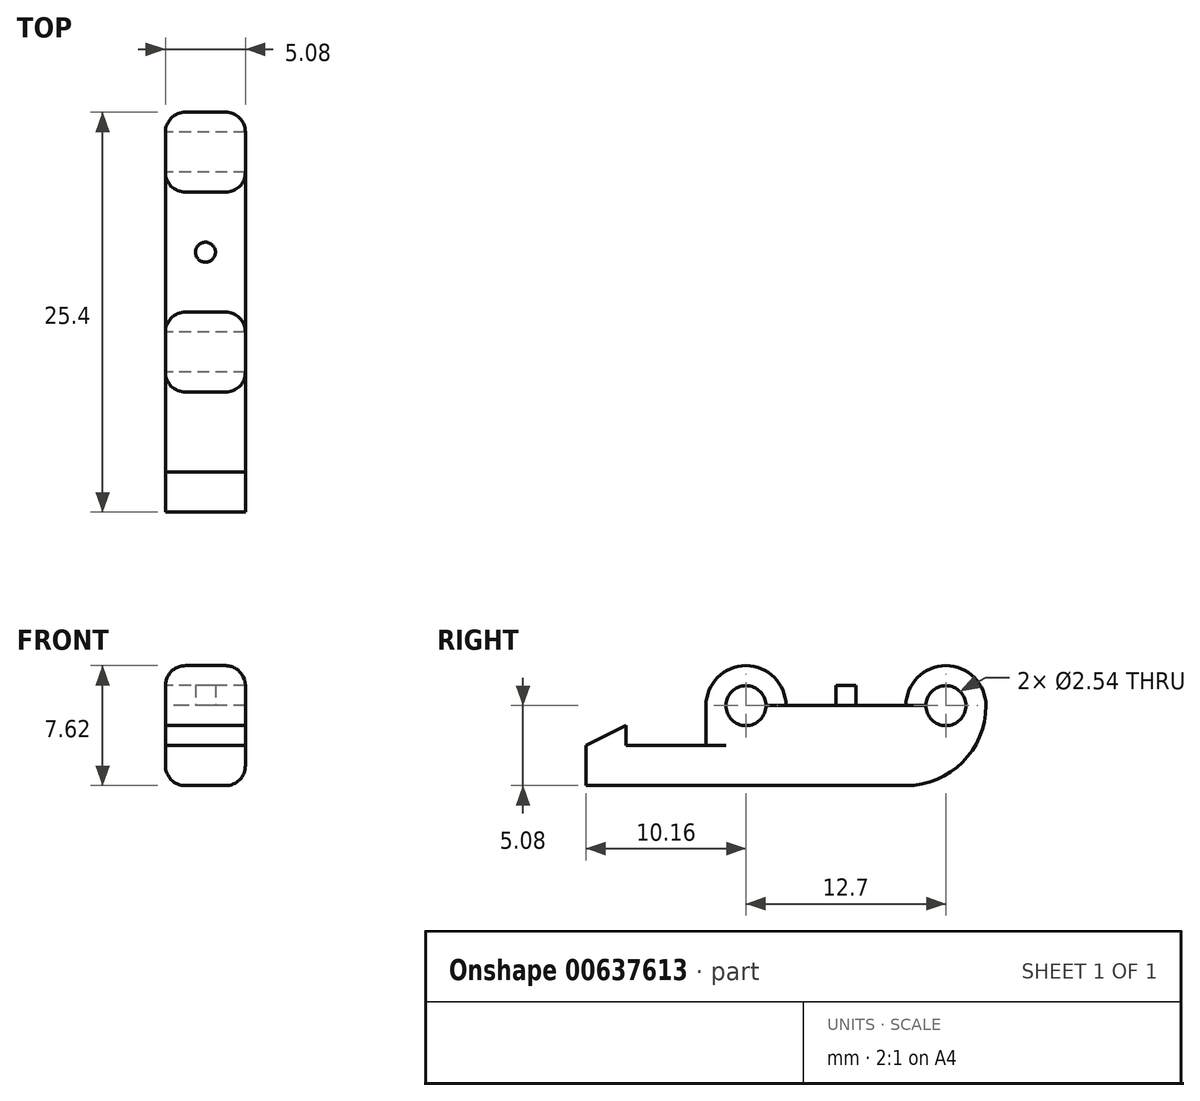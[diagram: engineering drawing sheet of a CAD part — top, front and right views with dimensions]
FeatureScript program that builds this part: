
annotation { "Feature Type Name" : "Feature", "Feature Type Description" : "" }
export const myFeature = defineFeature(function(context is Context, id is Id, definition is map)
    precondition{}
    {
        {
            var Q0;
            Q0=qCreatedBy(makeId("Right.planeOp"),FACE);
            var sketch = newSketch(context, id + "F0", { "sketchPlane" : qUnion([Q0])});
            skCircle(sketch, "E0", {"center": v(0, 0) * mm, "radius": 2.54 * mm});
            skCircle(sketch, "E1", {"center": v(0, 0) * mm, "radius": 1.27 * mm});
            skLineSegment(sketch, "E2", {"start": v(-2.54, 0) * mm, "end": v(-2.54, -5.08) * mm});
            skLineSegment(sketch, "E3", {"start": v(-2.54, -5.08) * mm, "end": v(15.24, -5.08) * mm});
            skLineSegment(sketch, "E4", {"start": v(15.24, -5.08) * mm, "end": v(15.24, 0) * mm});
            skCircle(sketch, "E5", {"center": v(12.7, 0) * mm, "radius": 2.54 * mm});
            skCircle(sketch, "E6", {"center": v(12.7, 0) * mm, "radius": 1.27 * mm});
            skLineSegment(sketch, "E7", {"start": v(10.16, 0) * mm, "end": v(10.16, 0) * mm});
            skLineSegment(sketch, "E8", {"start": v(2.54, 0) * mm, "end": v(2.54, 0) * mm});
            skLineSegment(sketch, "E9", {"start": v(2.54, 0) * mm, "end": v(10.16, 0) * mm});
            skLineSegment(sketch, "E10", {"start": v(-2.54, -5.08) * mm, "end": v(-10.16, -5.08) * mm});
            skLineSegment(sketch, "E11", {"start": v(-10.16, -5.08) * mm, "end": v(-10.16, -2.54) * mm});
            skLineSegment(sketch, "E12", {"start": v(-10.16, -2.54) * mm, "end": v(-2.54, -2.54) * mm});
            skLineSegment(sketch, "E13", {"start": v(-10.16, -2.54) * mm, "end": v(-7.62, -1.27) * mm});
            skLineSegment(sketch, "E14", {"start": v(-7.62, -1.27) * mm, "end": v(-7.62, -2.54) * mm});
            skSolve(sketch);
        }
        {
            var Q0;
            Q0=qSketchRegion(id+"F0",true);
            extrude(context, id + "F1", {"entities" : qUnion([Q0]), "depth" : 5.08 * mm});
        }
        {
            var Q0;
            Q0=makeQuery(id+"F1.opExtrude","SWEPT_FACE",FACE,{"disambiguationData":[OSD([sQuery(id+"F0.wireOp",EDGE,"E9")])]});
            var sketch = newSketch(context, id + "F2", { "sketchPlane" : qUnion([Q0])});
            skCircle(sketch, "E15", {"center": v(2.54, 6.35) * mm, "radius": 0.64 * mm});
            skPoint(sketch, "E15.centerSnap0", {"position": v(0, 6.35) * mm});
            skSolve(sketch);
        }
        {
            var Q0;
            Q0=qSketchRegion(id+"F2",true);
            extrude(context, id + "F3", {"entities" : qUnion([Q0]), "operationType" : NewBodyOperationType.ADD, "depth" : 1.27 * mm});
        }
        {
            var Q0;
            Q0=makeQuery(id+"F1.opExtrude","SWEPT_EDGE",EDGE,{"disambiguationData":[OSD([sQuery(id+"F0.wireOp",EDGE,"E3"),sQuery(id+"F0.wireOp",EDGE,"E4"),sQuery(id+"F0.wireOp",EDGE,"c4793016-eede-48da-aba7-3a384f1f3df9")])]});
            fillet(context, id + "F4", {"entities" : qUnion([Q0]), "radius" : 5.08 * mm, "tangentPropagation" : true, "allowEdgeOverflow" : false});
        }
        {
            var Q0;
            {var subQ0=sQuery(id+"F0.wireOp",EDGE,"E4");var subQ1=sQuery(id+"F0.wireOp",EDGE,"E3");Q0=makeQuery(id+"F4.opFillet","BLEND_EDGE",EDGE,{"blendedFrom":[makeQuery(id+"F1.opExtrude","SWEPT_EDGE",EDGE,{"disambiguationData":[OSD([subQ1,subQ0])]}),makeQuery(id+"F1.opExtrude","CAP_FACE",FACE,{"disambiguationData":[OSD([sQuery(id+"F0.wireOp",EDGE,"E0"),sQuery(id+"F0.wireOp",EDGE,"E1"),sQuery(id+"F0.wireOp",EDGE,"E2"),subQ1,subQ0,sQuery(id+"F0.wireOp",EDGE,"E5"),sQuery(id+"F0.wireOp",EDGE,"E6"),sQuery(id+"F0.wireOp",EDGE,"E9"),sQuery(id+"F0.wireOp",EDGE,"E10"),sQuery(id+"F0.wireOp",EDGE,"E11"),sQuery(id+"F0.wireOp",EDGE,"E12"),sQuery(id+"F0.wireOp",EDGE,"E13"),sQuery(id+"F0.wireOp",EDGE,"E14")])],"isStart":false})],"blendedInto":[makeQuery(id+"F1.opExtrude","CAP_FACE",FACE,{"disambiguationData":[OSD([sQuery(id+"F0.wireOp",EDGE,"E0"),sQuery(id+"F0.wireOp",EDGE,"E1"),sQuery(id+"F0.wireOp",EDGE,"E2"),subQ1,subQ0,sQuery(id+"F0.wireOp",EDGE,"E5"),sQuery(id+"F0.wireOp",EDGE,"E6"),sQuery(id+"F0.wireOp",EDGE,"E9"),sQuery(id+"F0.wireOp",EDGE,"E10"),sQuery(id+"F0.wireOp",EDGE,"E11"),sQuery(id+"F0.wireOp",EDGE,"E12"),sQuery(id+"F0.wireOp",EDGE,"E13"),sQuery(id+"F0.wireOp",EDGE,"E14")])],"isStart":false})]});}
            var Q1;
            {var subQ0=sQuery(id+"F0.wireOp",EDGE,"E4");var subQ1=sQuery(id+"F0.wireOp",EDGE,"E3");Q1=makeQuery(id+"F4.opFillet","BLEND_EDGE",EDGE,{"blendedFrom":[makeQuery(id+"F1.opExtrude","SWEPT_EDGE",EDGE,{"disambiguationData":[OSD([subQ1,subQ0])]}),makeQuery(id+"F1.opExtrude","CAP_FACE",FACE,{"disambiguationData":[OSD([sQuery(id+"F0.wireOp",EDGE,"E0"),sQuery(id+"F0.wireOp",EDGE,"E1"),sQuery(id+"F0.wireOp",EDGE,"E2"),subQ1,subQ0,sQuery(id+"F0.wireOp",EDGE,"E5"),sQuery(id+"F0.wireOp",EDGE,"E6"),sQuery(id+"F0.wireOp",EDGE,"E9"),sQuery(id+"F0.wireOp",EDGE,"E10"),sQuery(id+"F0.wireOp",EDGE,"E11"),sQuery(id+"F0.wireOp",EDGE,"E12"),sQuery(id+"F0.wireOp",EDGE,"E13"),sQuery(id+"F0.wireOp",EDGE,"E14")])],"isStart":true})],"blendedInto":[makeQuery(id+"F1.opExtrude","CAP_FACE",FACE,{"disambiguationData":[OSD([sQuery(id+"F0.wireOp",EDGE,"E0"),sQuery(id+"F0.wireOp",EDGE,"E1"),sQuery(id+"F0.wireOp",EDGE,"E2"),subQ1,subQ0,sQuery(id+"F0.wireOp",EDGE,"E5"),sQuery(id+"F0.wireOp",EDGE,"E6"),sQuery(id+"F0.wireOp",EDGE,"E9"),sQuery(id+"F0.wireOp",EDGE,"E10"),sQuery(id+"F0.wireOp",EDGE,"E11"),sQuery(id+"F0.wireOp",EDGE,"E12"),sQuery(id+"F0.wireOp",EDGE,"E13"),sQuery(id+"F0.wireOp",EDGE,"E14")])],"isStart":true})]});}
            var Q2;
            Q2=makeQuery(id+"F1.opExtrude","CAP_EDGE",EDGE,{"disambiguationData":[OSD([sQuery(id+"F0.wireOp",EDGE,"E0")])],"isStart":false});
            var Q3;
            Q3=makeQuery(id+"F1.opExtrude","CAP_EDGE",EDGE,{"disambiguationData":[OSD([sQuery(id+"F0.wireOp",EDGE,"E0")])],"isStart":true});
            fillet(context, id + "F5", {"entities" : qUnion([Q0, Q1, Q2, Q3]), "radius" : 1.27 * mm, "tangentPropagation" : true, "allowEdgeOverflow" : false});
        }
    });
